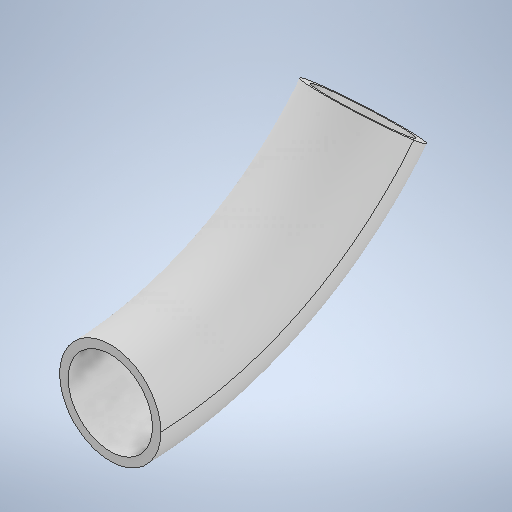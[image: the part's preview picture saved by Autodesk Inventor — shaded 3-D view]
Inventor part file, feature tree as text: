
AUTODESK INVENTOR PART (.ipt)
format: ipt  version: 2025.2 (Build 292293000, 293)  size: 316,928 bytes
history: native  units: mm
features: sketch x2, sweep x1
ambient origin geometry x8: Origin, YZ Plane, XZ Plane, XY Plane, X Axis, Y Axis, Z Axis, Center Point
bodies: Solid1 (feature_tree)
feature tree (3):
  sweep  "Sweep1"
  sketch  "Sketch1"  dims[d7=15.0mm d8=40.0mm]
  sketch  "Sketch2"  dims[d9=30.0mm d10=0.0mm d11=0.0mm d12=10.0mm d13=1.0mm]
